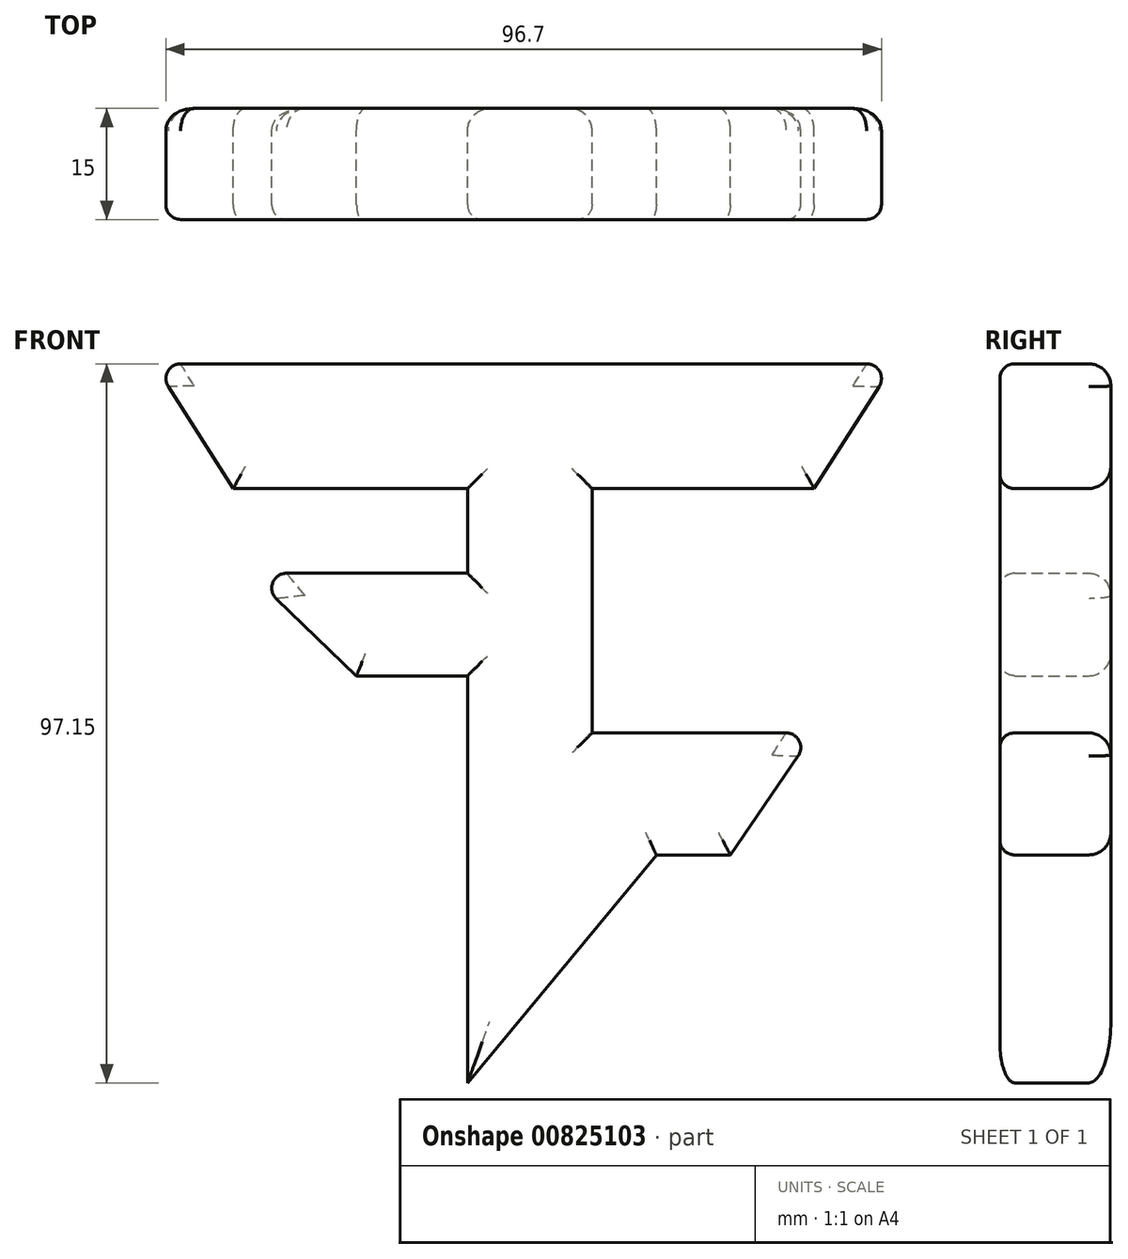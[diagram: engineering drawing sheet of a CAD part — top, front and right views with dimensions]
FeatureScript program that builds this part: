
annotation { "Feature Type Name" : "Feature", "Feature Type Description" : "" }
export const myFeature = defineFeature(function(context is Context, id is Id, definition is map)
    precondition{}
    {
        {
            var Q0;
            Q0=qCreatedBy(makeId("Front.planeOp"),FACE);
            var sketch = newSketch(context, id + "F0", { "sketchPlane" : qUnion([Q0])});
            skLineSegment(sketch, "E0", {"start": v(-50.95, 49.86) * mm, "end": v(49.05, 49.86) * mm});
            skLineSegment(sketch, "E1", {"start": v(49.05, 49.86) * mm, "end": v(38.3, 33) * mm});
            skLineSegment(sketch, "E2", {"start": v(38.3, 33) * mm, "end": v(8.3, 33) * mm});
            skLineSegment(sketch, "E3", {"start": v(8.3, 33) * mm, "end": v(8.3, 0) * mm});
            skLineSegment(sketch, "E4", {"start": v(8.3, 0) * mm, "end": v(38.3, 0) * mm});
            skLineSegment(sketch, "E5", {"start": v(38.3, 0) * mm, "end": v(26.99, -16.5) * mm});
            skLineSegment(sketch, "E6", {"start": v(26.99, -16.5) * mm, "end": v(16.99, -16.5) * mm});
            skLineSegment(sketch, "E7", {"start": v(16.99, -16.5) * mm, "end": v(-8.54, -47.3) * mm});
            skLineSegment(sketch, "E8", {"start": v(-8.54, -47.3) * mm, "end": v(-8.54, 7.7) * mm});
            skLineSegment(sketch, "E9", {"start": v(-8.54, 7.7) * mm, "end": v(-23.54, 7.7) * mm});
            skLineSegment(sketch, "E10", {"start": v(-23.54, 7.7) * mm, "end": v(-37.96, 21.56) * mm});
            skLineSegment(sketch, "E11", {"start": v(-37.96, 21.56) * mm, "end": v(-8.54, 21.56) * mm});
            skLineSegment(sketch, "E12", {"start": v(-8.54, 21.56) * mm, "end": v(-8.54, 33) * mm});
            skLineSegment(sketch, "E13", {"start": v(-50.95, 49.86) * mm, "end": v(-40.2, 33) * mm});
            skLineSegment(sketch, "E14", {"start": v(-40.2, 33) * mm, "end": v(-8.54, 33) * mm});
            skSolve(sketch);
        }
        {
            var Q0;
            Q0 = qSketchRegion(id + "F0", true);
            extrude(context, id + "F1", {"entities" : qUnion([Q0]), "depth" : 15 * mm, "offsetDistance" : 25 * mm});
        }
        {
            var Q0;
            Q0=makeQuery(id+"F1.opExtrude","SWEPT_EDGE",EDGE,{"disambiguationData":[OSD([sQuery(id+"F0.wireOp",EDGE,"E0"),sQuery(id+"F0.wireOp",EDGE,"E1")])]});
            var Q1;
            Q1=makeQuery(id+"F1.opExtrude","SWEPT_EDGE",EDGE,{"disambiguationData":[OSD([sQuery(id+"F0.wireOp",EDGE,"E0"),sQuery(id+"F0.wireOp",EDGE,"E13")])]});
            var Q2;
            Q2=makeQuery(id+"F1.opExtrude","CAP_EDGE",EDGE,{"disambiguationData":[OSD([sQuery(id+"F0.wireOp",EDGE,"E0")])],"isStart":false});
            var Q3;
            Q3=makeQuery(id+"F1.opExtrude","CAP_EDGE",EDGE,{"disambiguationData":[OSD([sQuery(id+"F0.wireOp",EDGE,"E11")])],"isStart":false});
            var Q4;
            Q4=makeQuery(id+"F1.opExtrude","SWEPT_EDGE",EDGE,{"disambiguationData":[OSD([sQuery(id+"F0.wireOp",EDGE,"E10"),sQuery(id+"F0.wireOp",EDGE,"E11")])]});
            var Q5;
            Q5=makeQuery(id+"F1.opExtrude","CAP_EDGE",EDGE,{"disambiguationData":[OSD([sQuery(id+"F0.wireOp",EDGE,"E3")])],"isStart":false});
            var Q6;
            Q6=makeQuery(id+"F1.opExtrude","CAP_EDGE",EDGE,{"disambiguationData":[OSD([sQuery(id+"F0.wireOp",EDGE,"E4")])],"isStart":false});
            var Q7;
            Q7=makeQuery(id+"F1.opExtrude","SWEPT_EDGE",EDGE,{"disambiguationData":[OSD([sQuery(id+"F0.wireOp",EDGE,"E4"),sQuery(id+"F0.wireOp",EDGE,"E5")])]});
            var Q8;
            Q8=makeQuery(id+"F1.opExtrude","CAP_EDGE",EDGE,{"disambiguationData":[OSD([sQuery(id+"F0.wireOp",EDGE,"E9")])],"isStart":false});
            var Q9;
            Q9=makeQuery(id+"F1.opExtrude","CAP_EDGE",EDGE,{"disambiguationData":[OSD([sQuery(id+"F0.wireOp",EDGE,"E10")])],"isStart":false});
            var Q10;
            Q10=makeQuery(id+"F1.opExtrude","CAP_EDGE",EDGE,{"disambiguationData":[OSD([sQuery(id+"F0.wireOp",EDGE,"E6")])],"isStart":false});
            var Q11;
            Q11=makeQuery(id+"F1.opExtrude","CAP_EDGE",EDGE,{"disambiguationData":[OSD([sQuery(id+"F0.wireOp",EDGE,"E5")])],"isStart":false});
            var Q12;
            Q12=makeQuery(id+"F1.opExtrude","CAP_EDGE",EDGE,{"disambiguationData":[OSD([sQuery(id+"F0.wireOp",EDGE,"E7")])],"isStart":false});
            var Q13;
            Q13=makeQuery(id+"F1.opExtrude","CAP_EDGE",EDGE,{"disambiguationData":[OSD([sQuery(id+"F0.wireOp",EDGE,"E8")])],"isStart":false});
            var Q14;
            Q14=makeQuery(id+"F1.opExtrude","CAP_EDGE",EDGE,{"disambiguationData":[OSD([sQuery(id+"F0.wireOp",EDGE,"E12")])],"isStart":false});
            var Q15;
            Q15=makeQuery(id+"F1.opExtrude","CAP_EDGE",EDGE,{"disambiguationData":[OSD([sQuery(id+"F0.wireOp",EDGE,"E14")])],"isStart":false});
            var Q16;
            Q16=makeQuery(id+"F1.opExtrude","CAP_EDGE",EDGE,{"disambiguationData":[OSD([sQuery(id+"F0.wireOp",EDGE,"E13")])],"isStart":false});
            var Q17;
            Q17=makeQuery(id+"F1.opExtrude","CAP_EDGE",EDGE,{"disambiguationData":[OSD([sQuery(id+"F0.wireOp",EDGE,"E2")])],"isStart":false});
            var Q18;
            Q18=makeQuery(id+"F1.opExtrude","CAP_EDGE",EDGE,{"disambiguationData":[OSD([sQuery(id+"F0.wireOp",EDGE,"E1")])],"isStart":false});
            fillet(context, id + "F2", {"entities" : qUnion([Q0, Q1, Q2, Q3, Q4, Q5, Q6, Q7, Q8, Q9, Q10, Q11, Q12, Q13, Q14, Q15, Q16, Q17, Q18]), "radius" : 2 * mm, "tangentPropagation" : true, "allowEdgeOverflow" : false});
        }
        {
            var Q0;
            Q0=makeQuery(id+"F1.opExtrude","CAP_EDGE",EDGE,{"disambiguationData":[OSD([sQuery(id+"F0.wireOp",EDGE,"E0")])],"isStart":true});
            var Q1;
            Q1=makeQuery(id+"F1.opExtrude","CAP_EDGE",EDGE,{"disambiguationData":[OSD([sQuery(id+"F0.wireOp",EDGE,"E12")])],"isStart":true});
            var Q2;
            Q2=makeQuery(id+"F1.opExtrude","CAP_EDGE",EDGE,{"disambiguationData":[OSD([sQuery(id+"F0.wireOp",EDGE,"E3")])],"isStart":true});
            var Q3;
            Q3=makeQuery(id+"F1.opExtrude","CAP_EDGE",EDGE,{"disambiguationData":[OSD([sQuery(id+"F0.wireOp",EDGE,"E2")])],"isStart":true});
            var Q4;
            Q4=makeQuery(id+"F1.opExtrude","CAP_EDGE",EDGE,{"disambiguationData":[OSD([sQuery(id+"F0.wireOp",EDGE,"E14")])],"isStart":true});
            var Q5;
            Q5=makeQuery(id+"F1.opExtrude","CAP_EDGE",EDGE,{"disambiguationData":[OSD([sQuery(id+"F0.wireOp",EDGE,"E11")])],"isStart":true});
            var Q6;
            Q6=makeQuery(id+"F1.opExtrude","CAP_EDGE",EDGE,{"disambiguationData":[OSD([sQuery(id+"F0.wireOp",EDGE,"E9")])],"isStart":true});
            var Q7;
            Q7=makeQuery(id+"F1.opExtrude","CAP_EDGE",EDGE,{"disambiguationData":[OSD([sQuery(id+"F0.wireOp",EDGE,"E10")])],"isStart":true});
            var Q8;
            Q8=makeQuery(id+"F1.opExtrude","CAP_EDGE",EDGE,{"disambiguationData":[OSD([sQuery(id+"F0.wireOp",EDGE,"E8")])],"isStart":true});
            var Q9;
            Q9=makeQuery(id+"F1.opExtrude","CAP_EDGE",EDGE,{"disambiguationData":[OSD([sQuery(id+"F0.wireOp",EDGE,"E5")])],"isStart":true});
            var Q10;
            Q10=makeQuery(id+"F1.opExtrude","CAP_EDGE",EDGE,{"disambiguationData":[OSD([sQuery(id+"F0.wireOp",EDGE,"E6")])],"isStart":true});
            var Q11;
            Q11=makeQuery(id+"F1.opExtrude","CAP_EDGE",EDGE,{"disambiguationData":[OSD([sQuery(id+"F0.wireOp",EDGE,"E7")])],"isStart":true});
            var Q12;
            Q12=makeQuery(id+"F1.opExtrude","CAP_FACE",FACE,{"disambiguationData":[OSD([sQuery(id+"F0.wireOp",EDGE,"E0"),sQuery(id+"F0.wireOp",EDGE,"E1"),sQuery(id+"F0.wireOp",EDGE,"E2"),sQuery(id+"F0.wireOp",EDGE,"E3"),sQuery(id+"F0.wireOp",EDGE,"E4"),sQuery(id+"F0.wireOp",EDGE,"E5"),sQuery(id+"F0.wireOp",EDGE,"E6"),sQuery(id+"F0.wireOp",EDGE,"E7"),sQuery(id+"F0.wireOp",EDGE,"E8"),sQuery(id+"F0.wireOp",EDGE,"E9"),sQuery(id+"F0.wireOp",EDGE,"E10"),sQuery(id+"F0.wireOp",EDGE,"E11"),sQuery(id+"F0.wireOp",EDGE,"E12"),sQuery(id+"F0.wireOp",EDGE,"E13"),sQuery(id+"F0.wireOp",EDGE,"E14")])],"isStart":true});
            var Q13;
            Q13=makeQuery(id+"F1.opExtrude","CAP_FACE",FACE,{"disambiguationData":[OSD([sQuery(id+"F0.wireOp",EDGE,"E0"),sQuery(id+"F0.wireOp",EDGE,"E1"),sQuery(id+"F0.wireOp",EDGE,"E2"),sQuery(id+"F0.wireOp",EDGE,"E3"),sQuery(id+"F0.wireOp",EDGE,"E4"),sQuery(id+"F0.wireOp",EDGE,"E5"),sQuery(id+"F0.wireOp",EDGE,"E6"),sQuery(id+"F0.wireOp",EDGE,"E7"),sQuery(id+"F0.wireOp",EDGE,"E8"),sQuery(id+"F0.wireOp",EDGE,"E9"),sQuery(id+"F0.wireOp",EDGE,"E10"),sQuery(id+"F0.wireOp",EDGE,"E11"),sQuery(id+"F0.wireOp",EDGE,"E12"),sQuery(id+"F0.wireOp",EDGE,"E13"),sQuery(id+"F0.wireOp",EDGE,"E14")])],"isStart":false});
            fillet(context, id + "F3", {"entities" : qUnion([Q0, Q1, Q2, Q3, Q4, Q5, Q6, Q7, Q8, Q9, Q10, Q11, Q12, Q13]), "tangentPropagation" : true, "radius" : 3 * mm, "defaultsChanged" : true, "vertexSettings" : [], "allowEdgeOverflow" : false});
        }
    });
